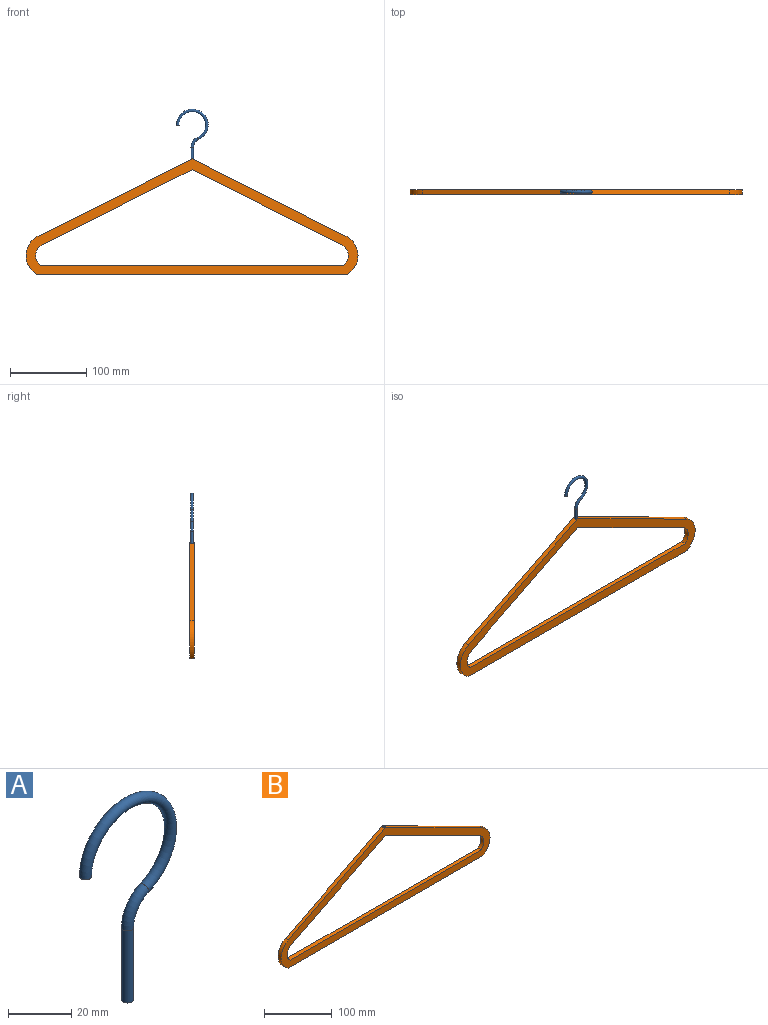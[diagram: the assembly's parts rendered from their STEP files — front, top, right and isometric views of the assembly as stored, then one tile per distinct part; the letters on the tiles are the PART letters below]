
ASSEMBLY  parts=2 mates=1
PART A: 5 faces, bbox 45.4x3.8x79.8 mm
  f0: plane 3.81x3.81mm, normal (0,0,-1), area 11.4mm2, adj f2
  f1: plane 3.81x3.81mm, normal (0,0,-1), area 11.4mm2, adj f4
  f2: cylinder r=1.91mm len=27.95mm, axis (0,0,1), area 334.6mm2, adj f0,f3
  f3: torus R=12.7mm, axis (0,1,0), area 177.4mm2, adj f2,f4
  f4: torus R=19.05mm, axis (0,-1,0), area 982.4mm2, adj f1,f3
PART B: 14 faces, bbox 436.5x6.4x152.4 mm
  f0: plane 202.36x101.6mm, normal (0.45,0,0.89), area 1431.5mm2, adj f1,f9,f10,f11,f12
  f1: plane 202.53x101.6mm, normal (-0.45,0,0.89), area 1432.4mm2, adj f0,f2,f10,f11,f12
  f2: cylinder r=28.61mm len=50.8mm, axis (0,1,0), area 397mm2, adj f1,f3,f10,f11
  f3: plane 406.4x6.35mm, normal (0,0,-1), area 2580.6mm2, adj f2,f9,f10,f11
  f4: plane 196.83x98.74mm, normal (0.45,0,-0.89), area 1398.3mm2, adj f5,f8,f10,f11
  f5: plane 196.67x98.74mm, normal (-0.45,0,-0.89), area 1397.4mm2, adj f4,f6,f10,f11
  f6: cylinder r=15.97mm len=26.75mm, axis (0,1,0), area 203.1mm2, adj f5,f7,f10,f11
  f7: plane 398.97x6.35mm, normal (0,0,1), area 2533.5mm2, adj f6,f8,f10,f11
  f8: cylinder r=15.91mm len=26.75mm, axis (0,1,0), area 203.3mm2, adj f4,f7,f10,f11
  f9: cylinder r=28.67mm len=50.8mm, axis (0,1,0), area 396.5mm2, adj f0,f3,f10,f11
  f10: plane 436.48x152.4mm, normal (0,-1,0), area 11986.7mm2, adj f0,f1,f2,f3,f4,f5,f6,f7
  f11: plane 436.48x152.4mm, normal (0,1,0), area 11986.7mm2, adj f0,f1,f2,f3,f4,f5,f6,f7
  f12: cylinder r=1.91mm len=12.7mm, axis (0,0,1), area 144.7mm2, adj f0,f1,f13
  f13: cone r=0mm half-angle=59deg, axis (0,0,1), area 13.3mm2, adj f12
PLACE A t=(-38.87,23.45,135.65)mm
PLACE B t=(-38.87,26.62,-4.05)mm
MATE revolute A.f2 <-> B.f12  axis (0,0,-1) through (-38.87,23.45,135.65)mm
